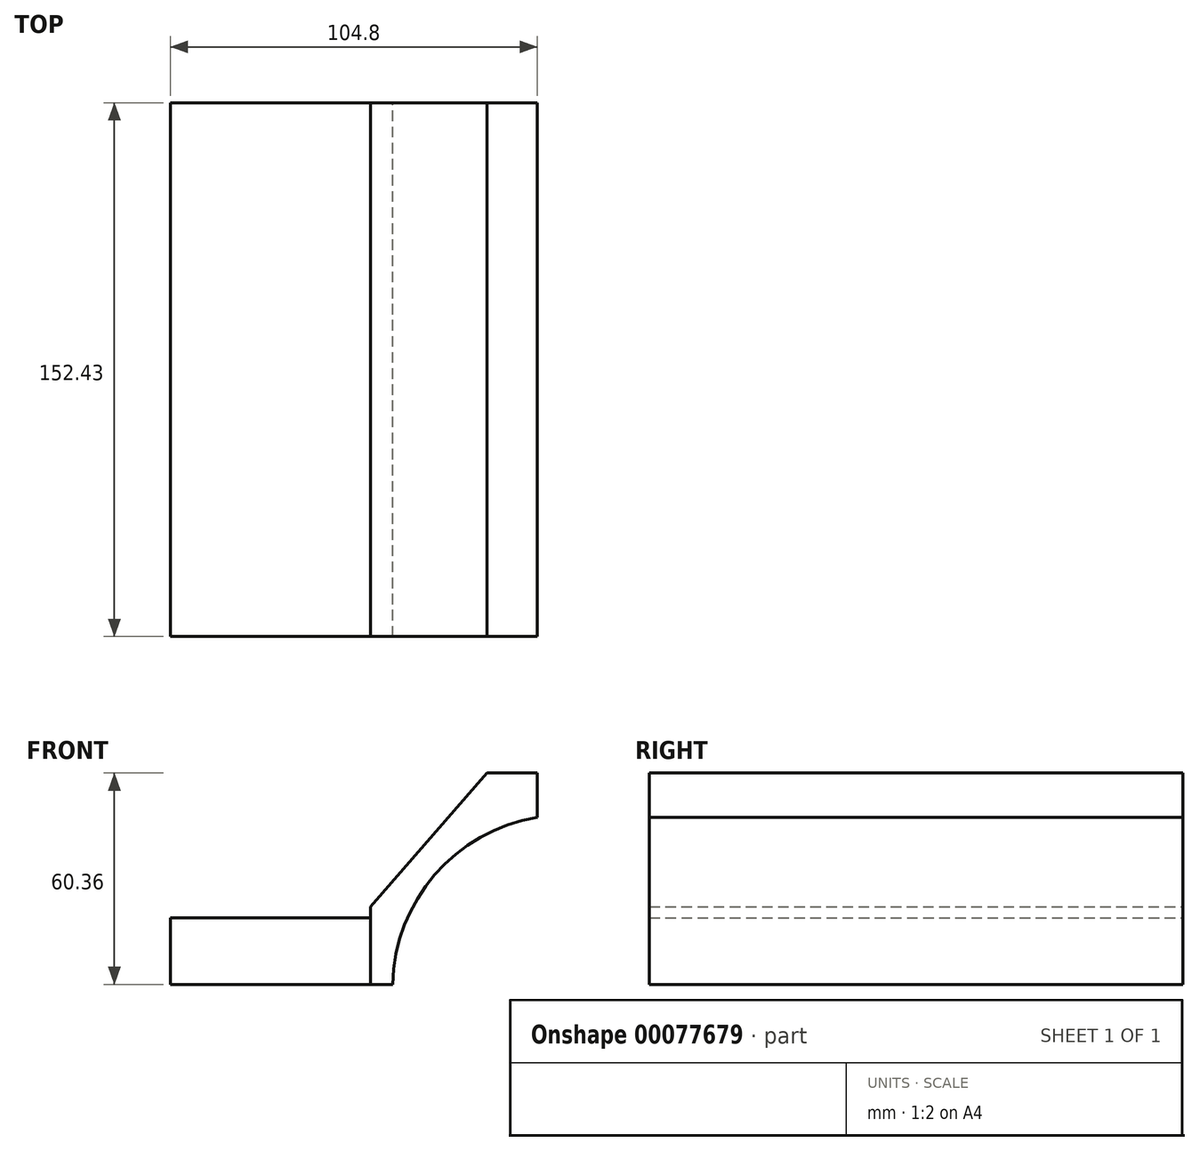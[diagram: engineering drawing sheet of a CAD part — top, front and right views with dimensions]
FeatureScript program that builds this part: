
annotation { "Feature Type Name" : "Feature", "Feature Type Description" : "" }
export const myFeature = defineFeature(function(context is Context, id is Id, definition is map)
    precondition{}
    {
        {
            var Q0;
            Q0=qCreatedBy(makeId("Front.planeOp"),FACE);
            var sketch = newSketch(context, id + "F0", { "sketchPlane" : qUnion([Q0])});
            skLineSegment(sketch, "E0", {"start": v(4.75, -30.18) * mm, "end": v(-52.4, -30.18) * mm});
            skLineSegment(sketch, "E1", {"start": v(-52.4, -30.18) * mm, "end": v(-52.4, -11.13) * mm});
            skLineSegment(sketch, "E2", {"start": v(-52.4, -11.13) * mm, "end": v(4.75, -11.13) * mm});
            skLineSegment(sketch, "E3", {"start": v(52.4, 30.18) * mm, "end": v(52.4, 17.47) * mm});
            skLineSegment(sketch, "E4", {"start": v(4.75, -30.18) * mm, "end": v(11.1, -30.18) * mm});
            skLineSegment(sketch, "E5", {"start": v(4.75, -30.18) * mm, "end": v(4.75, -7.94) * mm});
            skLineSegment(sketch, "E6", {"start": v(4.75, -7.94) * mm, "end": v(38.03, 30.18) * mm});
            skLineSegment(sketch, "E7", {"start": v(38.03, 30.18) * mm, "end": v(52.4, 30.18) * mm});
            skArc(sketch, "E8", {"start": v(52.4, 17.47) * mm, "mid": v(23.13, 1.12) * mm, "end": v(11.1, -30.18) * mm});
            skSolve(sketch);
        }
        {
            var Q0;
            {var subQ0=sQuery(id+"F0.wireOp",EDGE,"E0");Q0=makeQuery(id+"F0.imprint","IMPRINT",FACE,{"disambiguationData":[TD([[makeQuery(id+"F0.imprint","IMPRINT",EDGE,{"derivedFrom":subQ0}),-1.0]])]});}
            extrude(context, id + "F1", {"entities" : qUnion([Q0]), "depth" : 152.4 * mm});
        }
        {
            var Q0;
            Q0=makeQuery(id+"F0.imprint","IMPRINT",FACE,{"disambiguationData":[TD([[makeQuery(id+"F0.imprint","IMPRINT",EDGE,{"derivedFrom":sQuery(id+"F0.wireOp",EDGE,"E3")}),-1.0]])]});
            extrude(context, id + "F2", {"entities" : qUnion([Q0]), "operationType" : NewBodyOperationType.ADD, "depth" : 152.43 * mm});
        }
    });
